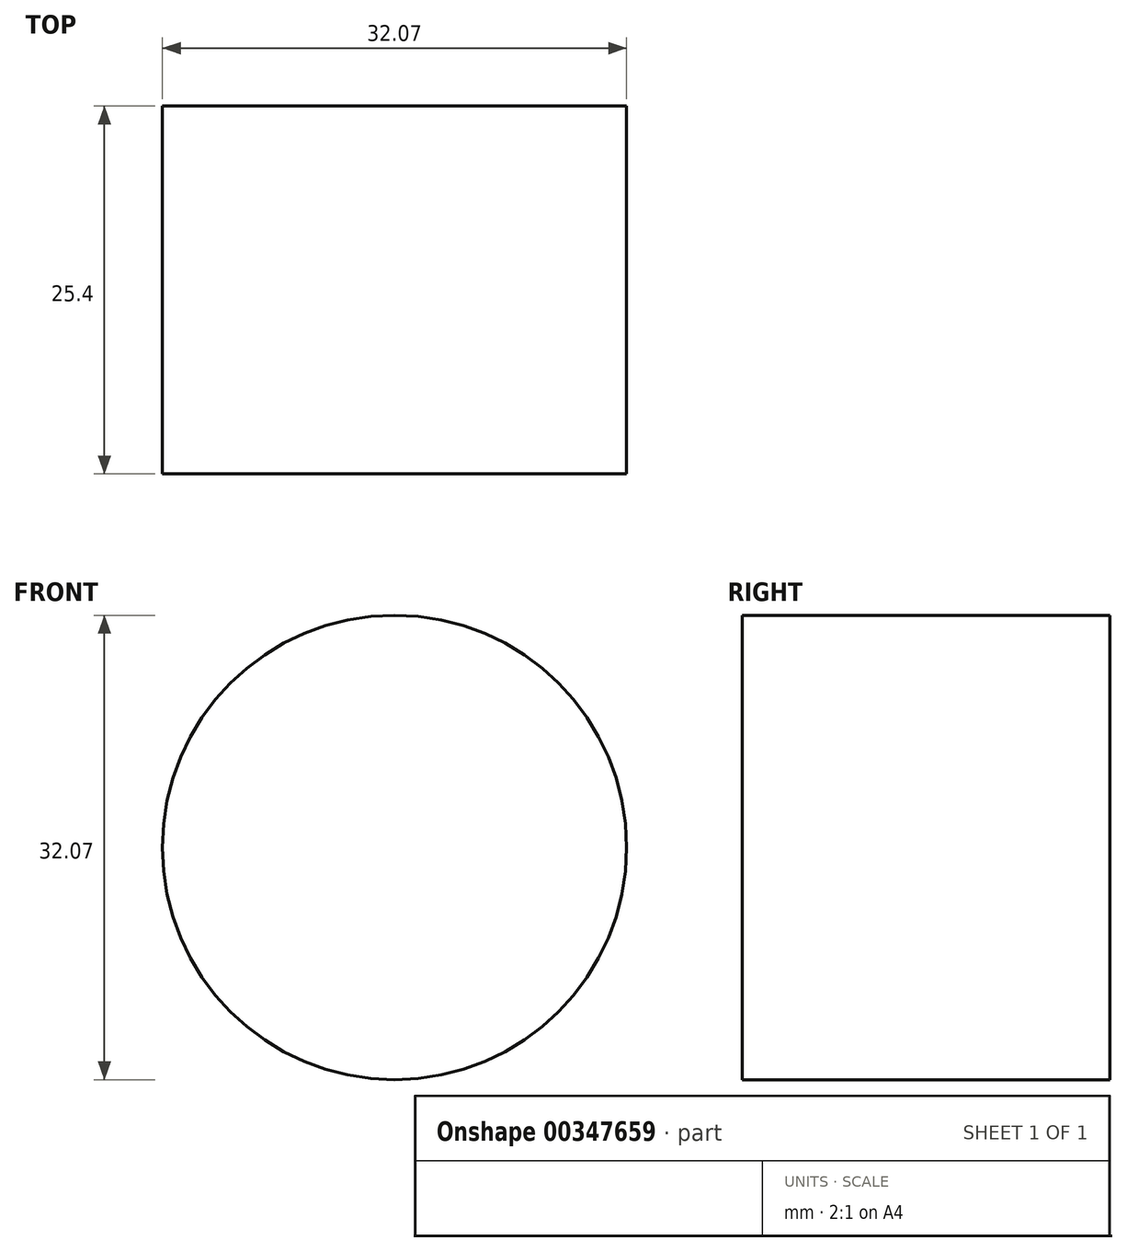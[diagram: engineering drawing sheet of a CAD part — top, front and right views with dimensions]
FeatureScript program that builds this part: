
annotation { "Feature Type Name" : "Feature", "Feature Type Description" : "" }
export const myFeature = defineFeature(function(context is Context, id is Id, definition is map)
    precondition{}
    {
        {
            var Q0;
            Q0=qCreatedBy(makeId("Front.planeOp"),FACE);
            var sketch = newSketch(context, id + "F0", { "sketchPlane" : qUnion([Q0])});
            skCircle(sketch, "E0", {"center": v(31.39, 43.55) * mm, "radius": 16.04 * mm});
            skSolve(sketch);
        }
        {
            var Q0;
            Q0=makeQuery(id+"F0.imprint","IMPRINT",FACE,{"disambiguationData":[TD([[makeQuery(id+"F0.imprint","IMPRINT",EDGE,{"derivedFrom":sQuery(id+"F0.wireOp",EDGE,"E0")}),1.0]])]});
            extrude(context, id + "F1", {"entities" : qUnion([Q0]), "depth" : 25.4 * mm});
        }
    });
